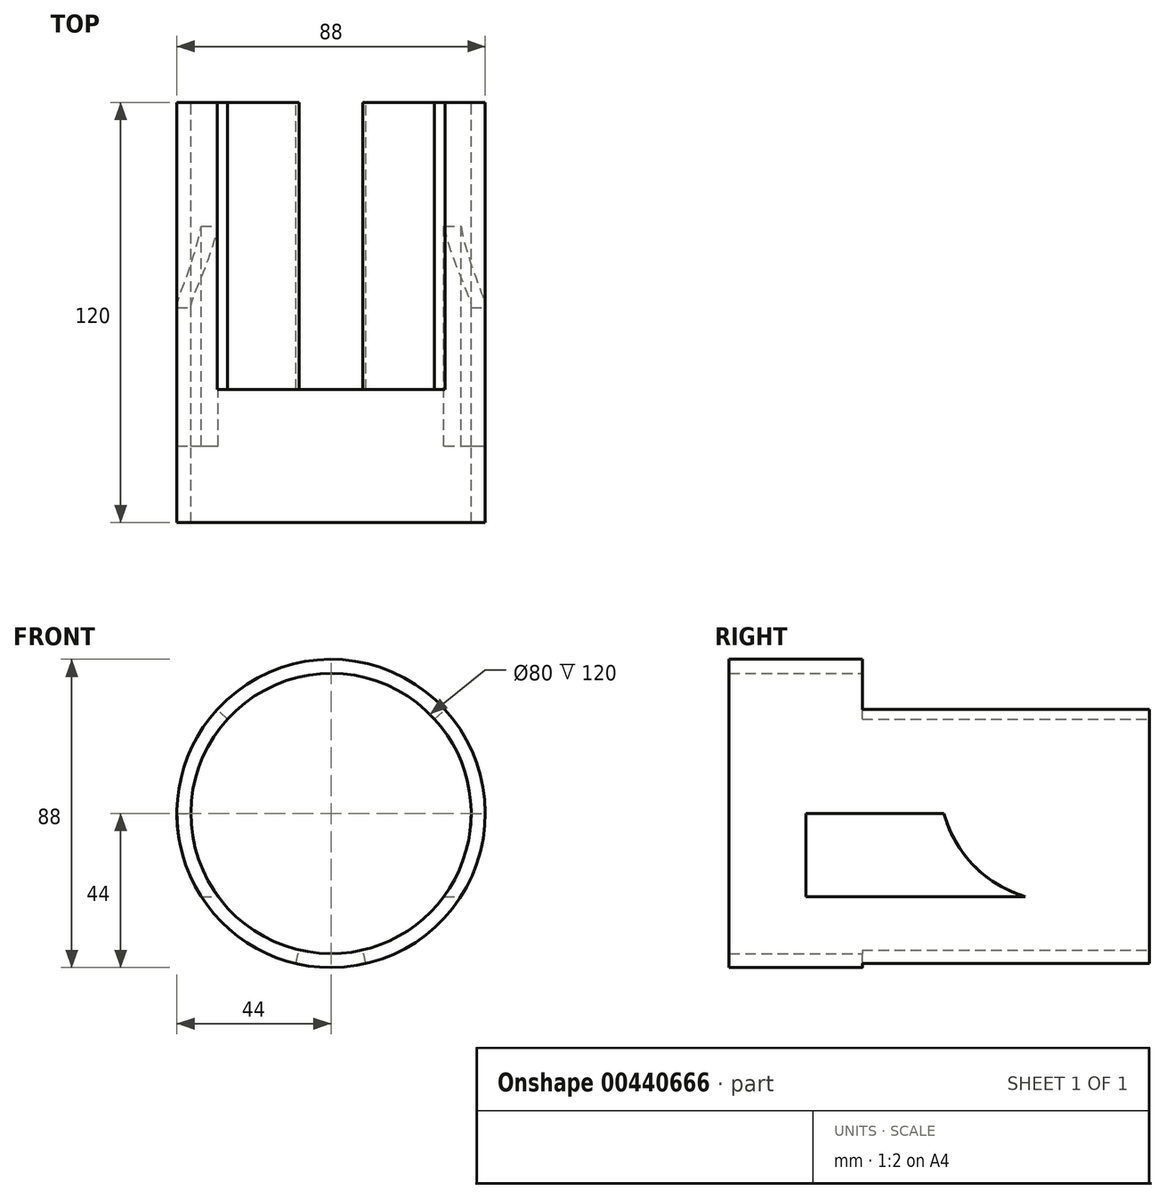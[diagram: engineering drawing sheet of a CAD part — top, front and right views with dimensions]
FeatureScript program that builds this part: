
annotation { "Feature Type Name" : "Feature", "Feature Type Description" : "" }
export const myFeature = defineFeature(function(context is Context, id is Id, definition is map)
    precondition{}
    {
        {
            var Q0;
            Q0=qCreatedBy(makeId("Front.planeOp"),FACE);
            var sketch = newSketch(context, id + "F0", { "sketchPlane" : qUnion([Q0])});
            skCircle(sketch, "E0", {"center": v(0, 0) * mm, "radius": 44 * mm});
            skCircle(sketch, "E1", {"center": v(0, 0) * mm, "radius": 40 * mm});
            skSolve(sketch);
        }
        {
            var Q0;
            Q0 = qSketchRegion(id + "F0", true);
            extrude(context, id + "F1", {"entities" : qUnion([Q0]), "depth" : 120 * mm});
        }
        {
            var Q0;
            Q0=makeQuery(id+"F1.opExtrude","CAP_FACE",FACE,{"disambiguationData":[OSD([sQuery(id+"F0.wireOp",EDGE,"E0"),sQuery(id+"F0.wireOp",EDGE,"E1")])],"isStart":true});
            var sketch = newSketch(context, id + "F2", { "sketchPlane" : qUnion([Q0])});
            skLineSegment(sketch, "E2", {"start": v(-40.32, 26.84) * mm, "end": v(-40.32, 26.05) * mm});
            skPoint(sketch, "E3.orphan", {"position": v(-32.5, 7.16) * mm});
            skPoint(sketch, "E4.orphan", {"position": v(32.5, 7.16) * mm});
            skPoint(sketch, "E5.MirrorCS.start.orphan", {"position": v(0, 55.6) * mm});
            skPoint(sketch, "E6.start.orphan", {"position": v(-32.5, 55.6) * mm});
            skPoint(sketch, "E7.start.orphan", {"position": v(32.5, 55.6) * mm});
            skPoint(sketch, "E8.start.orphan", {"position": v(32.5, 29.66) * mm});
            skPoint(sketch, "E9.end.orphan", {"position": v(10, -49.13) * mm});
            skPoint(sketch, "E9.start.orphan", {"position": v(0, -49.13) * mm});
            skPoint(sketch, "E10.start.orphan", {"position": v(-10, -49.13) * mm});
            skLineSegment(sketch, "E11", {"start": v(-10, -42.85) * mm, "end": v(-9.08, -38.89) * mm});
            skLineSegment(sketch, "E12", {"start": v(-29.5, 26.92) * mm, "end": v(-32.5, 29.66) * mm});
            skLineSegment(sketch, "E13.MirrorCS", {"start": v(10, -42.85) * mm, "end": v(9.08, -38.89) * mm});
            skLineSegment(sketch, "E14.MirrorCS", {"start": v(29.5, 26.92) * mm, "end": v(32.5, 29.66) * mm});
            skArc(sketch, "E15", {"start": v(-9.08, -38.89) * mm, "mid": v(0, -39.93) * mm, "end": v(9.08, -38.89) * mm});
            skArc(sketch, "E16.trimOffspring", {"start": v(29.5, 26.92) * mm, "mid": v(0, 39.93) * mm, "end": v(-29.5, 26.92) * mm});
            skArc(sketch, "E17", {"start": v(-10, -42.85) * mm, "mid": v(0, -44.05) * mm, "end": v(10, -42.85) * mm});
            skArc(sketch, "E18", {"start": v(32.5, 29.66) * mm, "mid": v(0, 44.08) * mm, "end": v(-32.5, 29.66) * mm});
            skSolve(sketch);
        }
        {
            var Q0;
            Q0 = qSketchRegion(id + "F2", true);
            extrude(context, id + "F3", {"entities" : qUnion([Q0]), "operationType" : NewBodyOperationType.REMOVE, "oppositeDirection" : true, "depth" : 82 * mm});
        }
        {
            var Q0;
            Q0=qCreatedBy(makeId("Right.planeOp"),FACE);
            var sketch = newSketch(context, id + "F4", { "sketchPlane" : qUnion([Q0])});
            skLineSegment(sketch, "E19", {"start": v(-98.11, 0) * mm, "end": v(-98.11, -23.7) * mm});
            skLineSegment(sketch, "E20", {"start": v(-98.11, -23.7) * mm, "end": v(-35.42, -23.7) * mm});
            skLineSegment(sketch, "E21", {"start": v(-98.11, 0) * mm, "end": v(-58.66, 0) * mm});
            skArc(sketch, "E22", {"start": v(-58.66, 0) * mm, "mid": v(-50.16, -14.9) * mm, "end": v(-35.42, -23.7) * mm});
            skSolve(sketch);
        }
        {
            var Q0;
            Q0 = qSketchRegion(id + "F4", true);
            extrude(context, id + "F5", {"entities" : qUnion([Q0]), "operationType" : NewBodyOperationType.REMOVE, "endBound" : BoundingType.SYMMETRIC, "oppositeDirection" : true, "depth" : 125 * mm});
        }
    });
